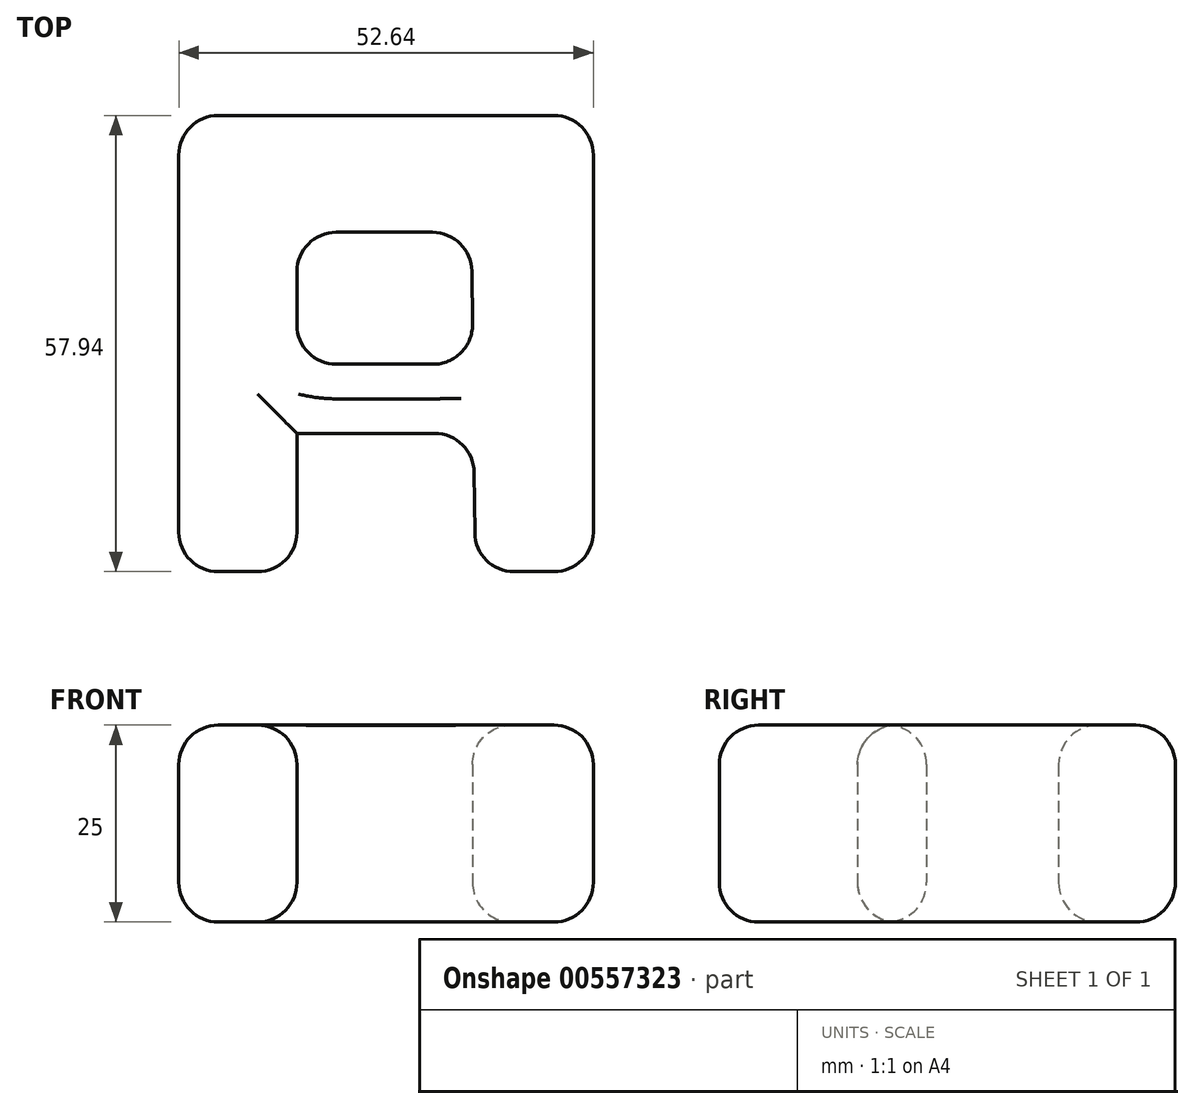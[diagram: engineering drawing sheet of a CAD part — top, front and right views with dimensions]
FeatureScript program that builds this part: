
annotation { "Feature Type Name" : "Feature", "Feature Type Description" : "" }
export const myFeature = defineFeature(function(context is Context, id is Id, definition is map)
    precondition{}
    {
        {
            var Q0;
            Q0=qCreatedBy(makeId("Top.planeOp"),FACE);
            var sketch = newSketch(context, id + "F0", { "sketchPlane" : qUnion([Q0])});
            skLineSegment(sketch, "E0", {"start": v(-26.32, 57.94) * mm, "end": v(-26.32, 0) * mm});
            skLineSegment(sketch, "E1", {"start": v(-26.32, 0) * mm, "end": v(-11.32, 0) * mm});
            skLineSegment(sketch, "E2", {"start": v(-26.32, 57.94) * mm, "end": v(-2.2, 57.94) * mm});
            skLineSegment(sketch, "E3.MirrorCS", {"start": v(26.32, 57.94) * mm, "end": v(2.2, 57.94) * mm});
            skLineSegment(sketch, "E4.MirrorCS", {"start": v(26.32, 57.94) * mm, "end": v(26.32, 0) * mm});
            skLineSegment(sketch, "E5", {"start": v(11.32, 0) * mm, "end": v(26.32, 0) * mm});
            skLineSegment(sketch, "E6", {"start": v(-11.32, 43.1) * mm, "end": v(10.84, 43.1) * mm});
            skLineSegment(sketch, "E7", {"start": v(10.84, 43.1) * mm, "end": v(11.32, 0) * mm});
            skLineSegment(sketch, "E8", {"start": v(-11.32, 43.1) * mm, "end": v(-11.32, 0) * mm});
            skLineSegment(sketch, "E9", {"start": v(86.75, -6.43) * mm, "end": v(86.72, -4.44) * mm});
            skLineSegment(sketch, "E10", {"start": v(-2.2, 57.94) * mm, "end": v(4.22, 57.94) * mm});
            skLineSegment(sketch, "E11", {"start": v(-11.32, 26.34) * mm, "end": v(11.03, 26.34) * mm});
            skLineSegment(sketch, "E12", {"start": v(-11.32, 17.56) * mm, "end": v(11.13, 17.56) * mm});
            skPoint(sketch, "E13.start.orphan", {"position": v(0, 57.94) * mm});
            skLineSegment(sketch, "E14.bottom", {"start": v(-11.32, 26.34) * mm, "end": v(11.13, 26.34) * mm});
            skLineSegment(sketch, "E14.left", {"start": v(-11.32, 26.34) * mm, "end": v(-11.32, 17.56) * mm});
            skLineSegment(sketch, "E14.right", {"start": v(11.13, 26.34) * mm, "end": v(11.13, 17.56) * mm});
            skSolve(sketch);
        }
        {
            var Q0;
            Q0=makeQuery(id+"F0.imprint","IMPRINT",FACE,{"disambiguationData":[TD([[makeQuery(id+"F0.imprint","IMPRINT",EDGE,{"derivedFrom":sQuery(id+"F0.wireOp",EDGE,"E0")}),1.0]])]});
            extrude(context, id + "F1", {"entities" : qUnion([Q0]), "depth" : 25 * mm, "offsetDistance" : 25 * mm});
        }
        {
            var Q0;
            Q0 = qSketchRegion(id + "F0", true);
            extrude(context, id + "F2", {"entities" : qUnion([Q0]), "operationType" : NewBodyOperationType.ADD, "depth" : 25 * mm, "offsetDistance" : 25 * mm});
        }
        {
            var Q0;
            {var subQ0=sQuery(id+"F0.wireOp",EDGE,"E14.bottom");var subQ1=sQuery(id+"F0.wireOp",EDGE,"E10");var subQ2=sQuery(id+"F0.wireOp",EDGE,"E8");var subQ3=sQuery(id+"F0.wireOp",EDGE,"E7");var subQ4=sQuery(id+"F0.wireOp",EDGE,"E6");var subQ5=sQuery(id+"F0.wireOp",EDGE,"E5");var subQ6=sQuery(id+"F0.wireOp",EDGE,"E4.MirrorCS");var subQ7=sQuery(id+"F0.wireOp",EDGE,"E3.MirrorCS");var subQ8=sQuery(id+"F0.wireOp",EDGE,"E2");var subQ9=sQuery(id+"F0.wireOp",EDGE,"E1");var subQ10=sQuery(id+"F0.wireOp",EDGE,"E0");Q0=makeQuery(id+"F2.boolean.opBoolean","MERGE",FACE,{"derivedFrom":[makeQuery(id+"F1.opExtrude","CAP_FACE",FACE,{"disambiguationData":[OSD([subQ10,subQ9,subQ8,subQ7,subQ6,subQ5,subQ4,subQ3,subQ2,subQ1,subQ0,sQuery(id+"F0.wireOp",EDGE,"E14.left"),sQuery(id+"F0.wireOp",EDGE,"E14.right")])],"isStart":false}),makeQuery(id+"F2.opExtrude","CAP_FACE",FACE,{"disambiguationData":[OSD([subQ10,subQ9,subQ8,subQ7,subQ6,subQ5,subQ4,subQ3,subQ2,subQ1,subQ0,sQuery(id+"F0.wireOp",EDGE,"E12")])],"isStart":false})]});}
            var Q1;
            Q1=makeQuery(id+"F1.opExtrude","SWEPT_FACE",FACE,{"disambiguationData":[OSD([sQuery(id+"F0.wireOp",EDGE,"E2"),sQuery(id+"F0.wireOp",EDGE,"E3.MirrorCS"),sQuery(id+"F0.wireOp",EDGE,"E10")])]});
            var Q2;
            {var subQ0=sQuery(id+"F0.wireOp",EDGE,"E7");Q2=makeQuery(id+"F1.opExtrude","SWEPT_FACE",FACE,{"disambiguationData":[OSD([subQ0]),TDD([makeQuery(id+"F0.imprint","IMPRINT",EDGE,{"disambiguationData":[TD([[makeQuery(id+"F0.imprint","INTERSECT",VERTEX,{"derivedFrom":[sQuery(id+"F0.wireOp",EDGE,"E6"),subQ0]}),-1.0]])],"derivedFrom":subQ0})])]});}
            var Q3;
            Q3=makeQuery(id+"F1.opExtrude","SWEPT_FACE",FACE,{"disambiguationData":[OSD([sQuery(id+"F0.wireOp",EDGE,"E4.MirrorCS")])]});
            var Q4;
            {var subQ0=sQuery(id+"F0.wireOp",EDGE,"E14.bottom");var subQ1=sQuery(id+"F0.wireOp",EDGE,"E10");var subQ2=sQuery(id+"F0.wireOp",EDGE,"E8");var subQ3=sQuery(id+"F0.wireOp",EDGE,"E7");var subQ4=sQuery(id+"F0.wireOp",EDGE,"E6");var subQ5=sQuery(id+"F0.wireOp",EDGE,"E5");var subQ6=sQuery(id+"F0.wireOp",EDGE,"E4.MirrorCS");var subQ7=sQuery(id+"F0.wireOp",EDGE,"E3.MirrorCS");var subQ8=sQuery(id+"F0.wireOp",EDGE,"E2");var subQ9=sQuery(id+"F0.wireOp",EDGE,"E1");var subQ10=sQuery(id+"F0.wireOp",EDGE,"E0");Q4=makeQuery(id+"F2.boolean.opBoolean","MERGE",FACE,{"derivedFrom":[makeQuery(id+"F1.opExtrude","CAP_FACE",FACE,{"disambiguationData":[OSD([subQ10,subQ9,subQ8,subQ7,subQ6,subQ5,subQ4,subQ3,subQ2,subQ1,subQ0,sQuery(id+"F0.wireOp",EDGE,"E14.left"),sQuery(id+"F0.wireOp",EDGE,"E14.right")])],"isStart":true}),makeQuery(id+"F2.opExtrude","CAP_FACE",FACE,{"disambiguationData":[OSD([subQ10,subQ9,subQ8,subQ7,subQ6,subQ5,subQ4,subQ3,subQ2,subQ1,subQ0,sQuery(id+"F0.wireOp",EDGE,"E12")])],"isStart":true})]});}
            var Q5;
            Q5=makeQuery(id+"F1.opExtrude","CAP_EDGE",EDGE,{"disambiguationData":[OSD([sQuery(id+"F0.wireOp",EDGE,"E6")])],"isStart":false});
            var Q6;
            Q6=makeQuery(id+"F1.opExtrude","CAP_EDGE",EDGE,{"disambiguationData":[OSD([sQuery(id+"F0.wireOp",EDGE,"E1")])],"isStart":true});
            var Q7;
            Q7=makeQuery(id+"F1.opExtrude","SWEPT_FACE",FACE,{"disambiguationData":[OSD([sQuery(id+"F0.wireOp",EDGE,"E1")])]});
            var Q8;
            Q8=makeQuery(id+"F1.opExtrude","CAP_EDGE",EDGE,{"disambiguationData":[OSD([sQuery(id+"F0.wireOp",EDGE,"E5")])],"isStart":false});
            var Q9;
            Q9=makeQuery(id+"F1.opExtrude","CAP_EDGE",EDGE,{"disambiguationData":[OSD([sQuery(id+"F0.wireOp",EDGE,"E5")])],"isStart":true});
            var Q10;
            Q10=makeQuery(id+"F2.opExtrude","CAP_EDGE",EDGE,{"disambiguationData":[OSD([sQuery(id+"F0.wireOp",EDGE,"E12")])],"isStart":false});
            var Q11;
            Q11=makeQuery(id+"F1.opExtrude","SWEPT_EDGE",EDGE,{"disambiguationData":[OSD([sQuery(id+"F0.wireOp",EDGE,"E6"),sQuery(id+"F0.wireOp",EDGE,"E8")])]});
            var Q12;
            Q12=makeQuery(id+"F2.opExtrude","CAP_EDGE",EDGE,{"disambiguationData":[OSD([sQuery(id+"F0.wireOp",EDGE,"E14.bottom")])],"isStart":true});
            var Q13;
            Q13=makeQuery(id+"F2.opExtrude","SWEPT_EDGE",EDGE,{"disambiguationData":[OSD([sQuery(id+"F0.wireOp",EDGE,"E8"),sQuery(id+"F0.wireOp",EDGE,"E14.bottom"),sQuery(id+"F0.wireOp",EDGE,"E14.left")])]});
            var Q14;
            {var subQ0=sQuery(id+"F0.wireOp",EDGE,"E7");Q14=makeQuery(id+"F1.opExtrude","SWEPT_FACE",FACE,{"disambiguationData":[OSD([subQ0]),TDD([makeQuery(id+"F0.imprint","IMPRINT",EDGE,{"disambiguationData":[TD([[makeQuery(id+"F0.imprint","INTERSECT",VERTEX,{"derivedFrom":[sQuery(id+"F0.wireOp",EDGE,"E5"),subQ0]}),1.0]])],"derivedFrom":subQ0})])]});}
            var Q15;
            Q15=makeQuery(id+"F2.opExtrude","SWEPT_EDGE",EDGE,{"disambiguationData":[OSD([sQuery(id+"F0.wireOp",EDGE,"E8"),sQuery(id+"F0.wireOp",EDGE,"E12"),sQuery(id+"F0.wireOp",EDGE,"E14.left")])]});
            fillet(context, id + "F3", {"entities" : qUnion([Q0, Q1, Q2, Q3, Q4, Q5, Q6, Q7, Q8, Q9, Q10, Q11, Q12, Q13, Q14, Q15]), "radius" : 5 * mm, "tangentPropagation" : true, "allowEdgeOverflow" : false});
        }
    });
